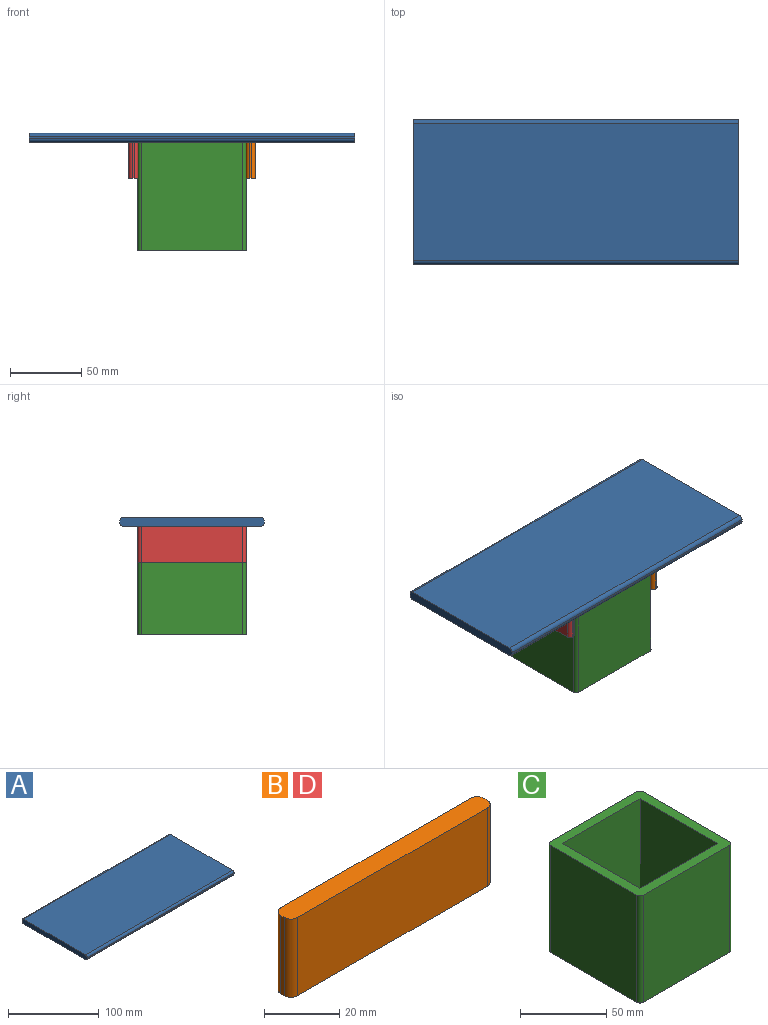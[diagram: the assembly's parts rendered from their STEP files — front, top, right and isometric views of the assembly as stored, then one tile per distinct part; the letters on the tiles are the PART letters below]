
ASSEMBLY  parts=4 mates=3
PART A: 10 faces, bbox 228.6x101.6x6.4 mm
  f0: plane 228.6x96.52mm, normal (0,0,1), area 22064.5mm2, adj f1,f3,f7,f9
  f1: plane 101.6x6.35mm, normal (-1,0,0), area 639.6mm2, adj f0,f2,f4,f5,f6,f7,f8,f9
  f2: plane 228.6x96.52mm, normal (0,0,-1), area 22064.5mm2, adj f1,f3,f6,f8
  f3: plane 101.6x6.35mm, normal (1,0,0), area 639.6mm2, adj f0,f2,f4,f5,f6,f7,f8,f9
  f4: plane 228.6x1.27mm, normal (0,-1,0), area 290.3mm2, adj f1,f3,f8,f9
  f5: plane 228.6x1.27mm, normal (0,1,0), area 290.3mm2, adj f1,f3,f6,f7
  f6: cylinder r=2.54mm len=228.6mm, axis (1,0,0), area 912.1mm2, adj f1,f2,f3,f5
  f7: cylinder r=2.54mm len=228.6mm, axis (-1,0,0), area 912.1mm2, adj f0,f1,f3,f5
  f8: cylinder r=2.54mm len=228.6mm, axis (-1,0,0), area 912.1mm2, adj f1,f2,f3,f4
  f9: cylinder r=2.54mm len=228.6mm, axis (1,0,0), area 912.1mm2, adj f0,f1,f3,f4
PART B: 10 faces, bbox 76.2x6.4x25.4 mm
  f0: plane 76.2x6.35mm, normal (0,0,1), area 478.3mm2, adj f1,f3,f4,f5,f6,f7,f8,f9
  f1: plane 25.4x1.27mm, normal (-1,0,0), area 32.3mm2, adj f0,f2,f6,f8
  f2: plane 76.2x6.35mm, normal (0,0,-1), area 478.3mm2, adj f1,f3,f4,f5,f6,f7,f8,f9
  f3: plane 25.4x1.27mm, normal (1,0,0), area 32.3mm2, adj f0,f2,f7,f9
  f4: plane 71.12x25.4mm, normal (0,-1,0), area 1806.4mm2, adj f0,f2,f8,f9
  f5: plane 71.12x25.4mm, normal (0,1,0), area 1806.4mm2, adj f0,f2,f6,f7
  f6: cylinder r=2.54mm len=25.4mm, axis (0,0,-1), area 101.3mm2, adj f0,f1,f2,f5
  f7: cylinder r=2.54mm len=25.4mm, axis (0,0,1), area 101.3mm2, adj f0,f2,f3,f5
  f8: cylinder r=2.54mm len=25.4mm, axis (0,0,1), area 101.3mm2, adj f0,f1,f2,f4
  f9: cylinder r=2.54mm len=25.4mm, axis (0,0,-1), area 101.3mm2, adj f0,f2,f3,f4
PART C: 14 faces, bbox 76.2x76.2x76.2 mm
  f0: plane 76.2x71.12mm, normal (0,1,0), area 5419.3mm2, adj f8,f9,f11,f12
  f1: plane 76.2x71.12mm, normal (-1,0,0), area 5419.3mm2, adj f8,f9,f10,f11
  f2: plane 76.2x71.12mm, normal (0,-1,0), area 5419.3mm2, adj f8,f9,f10,f13
  f3: plane 76.2x63.5mm, normal (1,0,0), area 4838.7mm2, adj f4,f6,f8,f9
  f4: plane 76.2x63.5mm, normal (0,-1,0), area 4838.7mm2, adj f3,f5,f8,f9
  f5: plane 76.2x63.5mm, normal (-1,0,0), area 4838.7mm2, adj f4,f6,f8,f9
  f6: plane 76.2x63.5mm, normal (0,1,0), area 4838.7mm2, adj f3,f5,f8,f9
  f7: plane 76.2x71.12mm, normal (1,0,0), area 5419.3mm2, adj f8,f9,f12,f13
  f8: plane 76.2x76.2mm, normal (0,0,1), area 1768.7mm2, adj f0,f1,f2,f3,f4,f5,f6,f7
  f9: plane 76.2x76.2mm, normal (0,0,-1), area 1768.7mm2, adj f0,f1,f2,f3,f4,f5,f6,f7
  f10: cylinder r=2.54mm len=76.2mm, axis (0,0,-1), area 304mm2, adj f1,f2,f8,f9
  f11: cylinder r=2.54mm len=76.2mm, axis (0,0,1), area 304mm2, adj f0,f1,f8,f9
  f12: cylinder r=2.54mm len=76.2mm, axis (0,0,-1), area 304mm2, adj f0,f7,f8,f9
  f13: cylinder r=2.54mm len=76.2mm, axis (0,0,1), area 304mm2, adj f2,f7,f8,f9
PART D: same geometry as B
PLACE A t=(-92.85,41.32,45.67)mm
PLACE B rot(axis=(0,0,-1),90deg) t=(12.22,-5.3,11.2)mm
PLACE C t=(-42.25,1.37,-24.41)mm
PLACE D rot(axis=(0,0,-1),90deg) t=(-70.33,-5.3,11.2)mm
MATE fastened A.f2 <-> C.f8  axis (0,0,-1) through (-32.23,-9.48,51.79)mm
MATE fastened D.f5 <-> C.f1  axis (1,0,0) through (-70.33,-9.48,51.79)mm
MATE fastened B.f4 <-> C.f7  axis (-1,0,0) through (5.87,-9.48,51.79)mm
